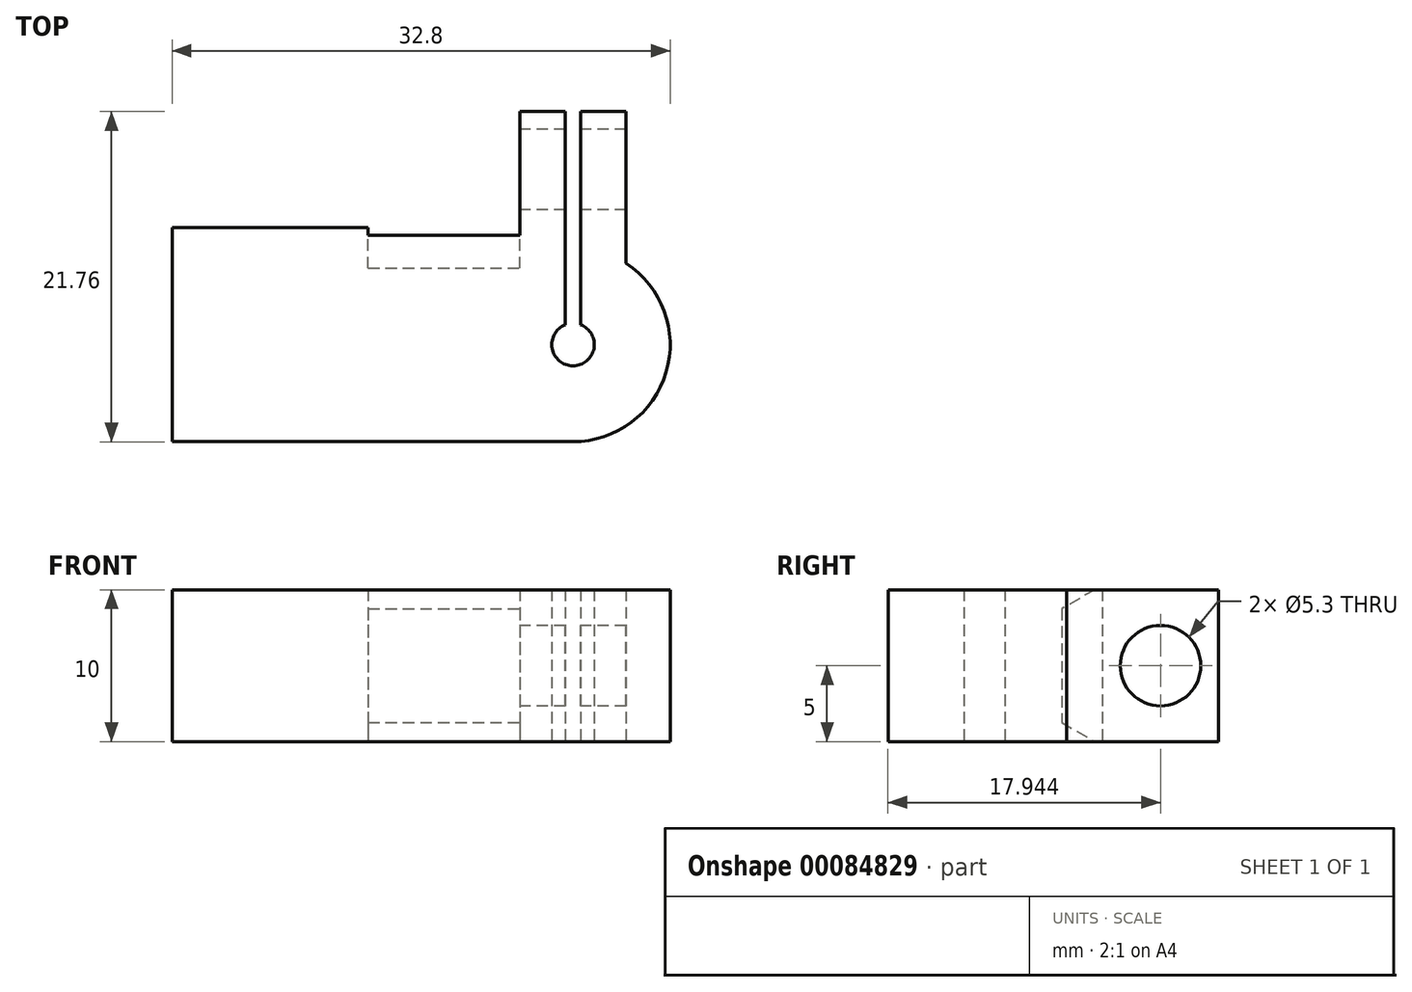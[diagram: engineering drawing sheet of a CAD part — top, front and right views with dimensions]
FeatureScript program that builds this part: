
annotation { "Feature Type Name" : "Feature", "Feature Type Description" : "" }
export const myFeature = defineFeature(function(context is Context, id is Id, definition is map)
    precondition{}
    {
        {
            var Q0;
            Q0=qCreatedBy(makeId("Top.planeOp"),FACE);
            var sketch = newSketch(context, id + "F0", { "sketchPlane" : qUnion([Q0])});
            skArc(sketch, "E0", {"start": v(-25.86, 22.73) * mm, "mid": v(-25.36, 20.02) * mm, "end": v(-24.86, 22.73) * mm});
            skArc(sketch, "E1", {"start": v(-25.36, 15.02) * mm, "mid": v(-19.23, 19.6) * mm, "end": v(-21.86, 26.78) * mm});
            skLineSegment(sketch, "E2.left", {"start": v(-25.86, 27.8) * mm, "end": v(-25.86, 22.73) * mm});
            skLineSegment(sketch, "E2.right", {"start": v(-24.86, 27.8) * mm, "end": v(-24.86, 22.73) * mm});
            skPoint(sketch, "E3.orphan", {"position": v(-25.86, 21.42) * mm});
            skPoint(sketch, "E4.orphan", {"position": v(-24.86, 21.42) * mm});
            skLineSegment(sketch, "E5.bottom", {"start": v(-28.86, 36.78) * mm, "end": v(-25.86, 36.78) * mm});
            skLineSegment(sketch, "E5.left", {"start": v(-28.86, 36.78) * mm, "end": v(-28.86, 29.15) * mm});
            skLineSegment(sketch, "E5.right", {"start": v(-25.86, 36.78) * mm, "end": v(-25.86, 26.78) * mm});
            skLineSegment(sketch, "E6.bottom", {"start": v(-24.86, 36.78) * mm, "end": v(-21.86, 36.78) * mm});
            skLineSegment(sketch, "E6.left", {"start": v(-24.86, 36.78) * mm, "end": v(-24.86, 26.78) * mm});
            skLineSegment(sketch, "E6.right", {"start": v(-21.86, 36.78) * mm, "end": v(-21.86, 26.78) * mm});
            skLineSegment(sketch, "E7.bottom", {"start": v(-31.76, 29.15) * mm, "end": v(-28.86, 29.15) * mm});
            skLineSegment(sketch, "E7.top", {"start": v(-31.76, 15.02) * mm, "end": v(-25.36, 15.02) * mm});
            skLineSegment(sketch, "E7.left", {"start": v(-31.76, 29.15) * mm, "end": v(-31.76, 15.02) * mm});
            skLineSegment(sketch, "E7.right", {"start": v(-25.36, 21.42) * mm, "end": v(-25.36, 15.02) * mm});
            skLineSegment(sketch, "E8.bottom", {"start": v(-31.76, 29.15) * mm, "end": v(-51.76, 29.15) * mm});
            skLineSegment(sketch, "E8.top", {"start": v(-31.76, 15.02) * mm, "end": v(-51.76, 15.02) * mm});
            skLineSegment(sketch, "E8.right", {"start": v(-51.76, 29.15) * mm, "end": v(-51.76, 15.02) * mm});
            skSolve(sketch);
        }
        {
            var Q0;
            Q0=makeQuery(id+"F0.imprint","IMPRINT",FACE,{"disambiguationData":[TD([[makeQuery(id+"F0.imprint","IMPRINT",EDGE,{"derivedFrom":sQuery(id+"F0.wireOp",EDGE,"E8.bottom")}),1.0]])]});
            var Q1;
            {var subQ5=sQuery(id+"F0.wireOp",EDGE,"E2.left");Q1=makeQuery(id+"F0.imprint","IMPRINT",FACE,{"disambiguationData":[TD([[makeQuery(id+"F0.imprint","IMPRINT",EDGE,{"derivedFrom":subQ5}),-1.0]])]});}
            var Q2;
            {var subQ5=sQuery(id+"F0.wireOp",EDGE,"E1");Q2=makeQuery(id+"F0.imprint","IMPRINT",FACE,{"disambiguationData":[TD([[makeQuery(id+"F0.imprint","IMPRINT",EDGE,{"derivedFrom":subQ5}),1.0]])]});}
            extrude(context, id + "F1", {"entities" : qUnion([Q0, Q1, Q2]), "depth" : 10 * mm});
        }
        {
            var Q0;
            Q0=makeQuery(id+"F1.opExtrude","SWEPT_FACE",FACE,{"disambiguationData":[OSD([sQuery(id+"F0.wireOp",EDGE,"E5.left")])]});
            var sketch = newSketch(context, id + "F2", { "sketchPlane" : qUnion([Q0])});
            skCircle(sketch, "E9", {"center": v(-32.96, 5) * mm, "radius": 2.65 * mm});
            skPoint(sketch, "E10", {"position": v(-32.96, 10) * mm});
            skPoint(sketch, "E11", {"position": v(-36.78, 5) * mm});
            skSolve(sketch);
        }
        {
            var Q0;
            Q0=makeQuery(id+"F2.imprint","IMPRINT",FACE,{"disambiguationData":[TD([[makeQuery(id+"F2.imprint","IMPRINT",EDGE,{"derivedFrom":sQuery(id+"F2.wireOp",EDGE,"E9")}),1.0]])]});
            extrude(context, id + "F3", {"entities" : qUnion([Q0]), "operationType" : NewBodyOperationType.REMOVE, "endBound" : BoundingType.THROUGH_ALL, "oppositeDirection" : true, "depth" : 25 * mm});
        }
        {
            var Q0;
            Q0=makeQuery(id+"F1.opExtrude","SWEPT_FACE",FACE,{"disambiguationData":[OSD([sQuery(id+"F0.wireOp",EDGE,"E5.left")])]});
            var sketch = newSketch(context, id + "F4", { "sketchPlane" : qUnion([Q0])});
            skCircle(sketch, "E12.cCircle", {"center": v(-32.96, 5) * mm, "radius": 6.5 * mm, "construction": true});
            skLineSegment(sketch, "E12.0", {"start": v(-39.46, 1.25) * mm, "end": v(-39.46, 8.75) * mm});
            skLineSegment(sketch, "E12.1", {"start": v(-39.46, 8.75) * mm, "end": v(-32.96, 12.5) * mm});
            skLineSegment(sketch, "E12.2", {"start": v(-32.96, 12.5) * mm, "end": v(-26.46, 8.75) * mm});
            skLineSegment(sketch, "E12.3", {"start": v(-26.46, 8.75) * mm, "end": v(-26.46, 1.25) * mm});
            skLineSegment(sketch, "E12.4", {"start": v(-26.46, 1.25) * mm, "end": v(-32.96, -2.5) * mm});
            skLineSegment(sketch, "E12.5", {"start": v(-32.96, -2.5) * mm, "end": v(-39.46, 1.25) * mm});
            skPoint(sketch, "E12.0.midPoint", {"position": v(-39.46, 5) * mm});
            skSolve(sketch);
        }
        {
            var Q0;
            Q0=makeQuery(id+"F4.imprint","IMPRINT",FACE,{"disambiguationData":[TD([[makeQuery(id+"F4.imprint","IMPRINT",EDGE,{"derivedFrom":sQuery(id+"F4.wireOp",EDGE,"E12.0")}),-1.0]])]});
            var Q1;
            {var subQ0=sQuery(id+"F0.wireOp",EDGE,"E5.left");Q1=makeQuery(id+"F4.imprint","IMPRINT",FACE,{"disambiguationData":[TD([[makeQuery(id+"F4.imprint","IMPRINT",EDGE,{"derivedFrom":makeQuery(id+"F1.opExtrude","CAP_EDGE",EDGE,{"disambiguationData":[OSD([subQ0])],"isStart":true})}),1.0]])]});}
            extrude(context, id + "F5", {"entities" : qUnion([Q0, Q1]), "operationType" : NewBodyOperationType.REMOVE, "depth" : 10 * mm});
        }
    });
